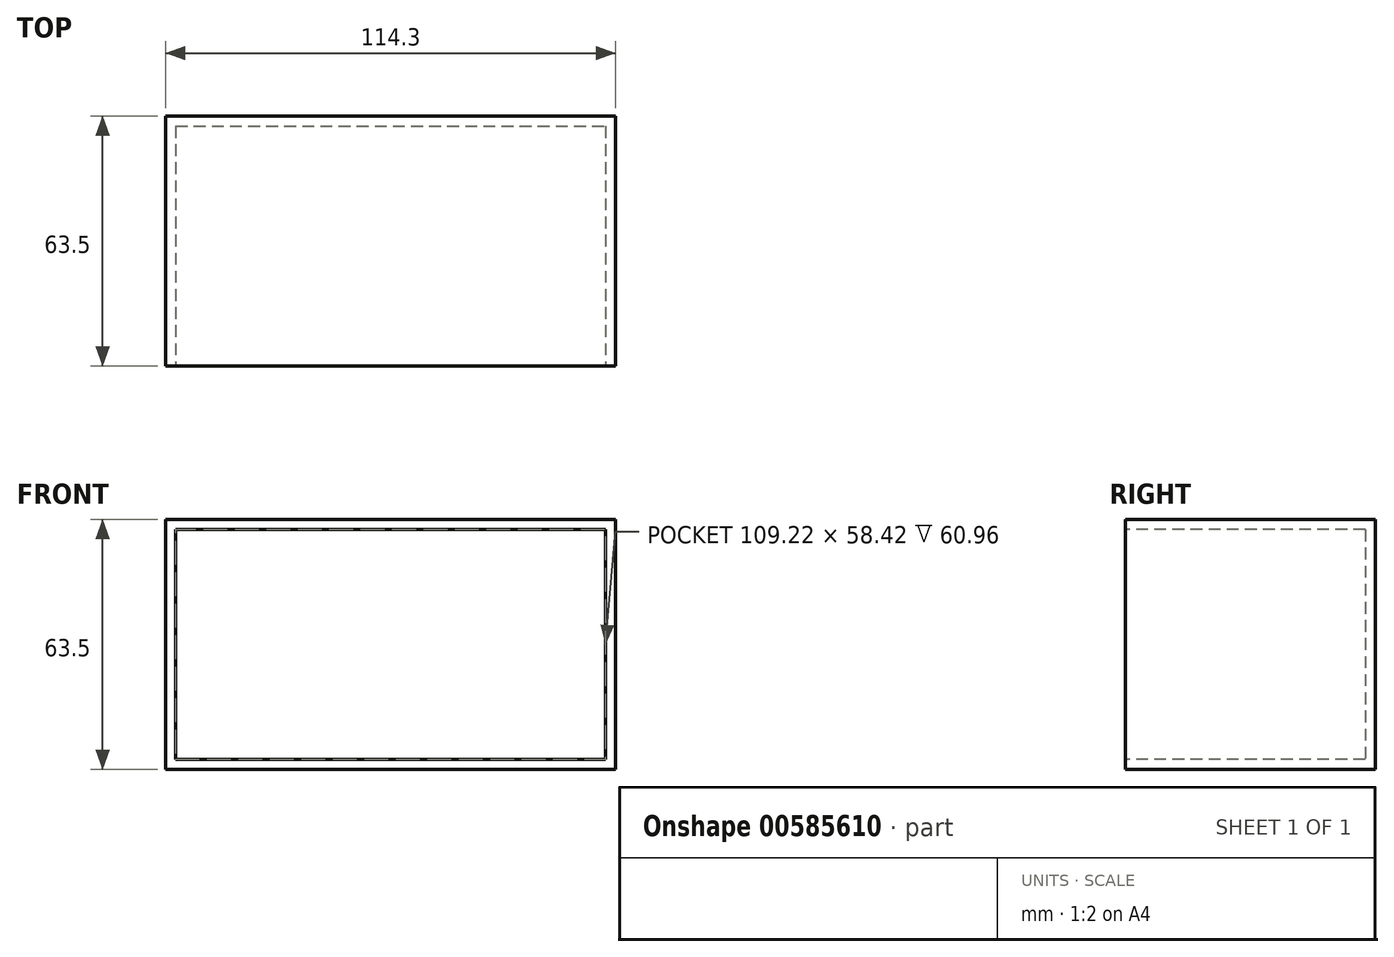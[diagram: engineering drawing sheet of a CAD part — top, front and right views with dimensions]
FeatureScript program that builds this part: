
annotation { "Feature Type Name" : "Feature", "Feature Type Description" : "" }
export const myFeature = defineFeature(function(context is Context, id is Id, definition is map)
    precondition{}
    {
        {
            var Q0;
            Q0=qCreatedBy(makeId("Top.planeOp"),FACE);
            var sketch = newSketch(context, id + "F0", { "sketchPlane" : qUnion([Q0])});
            skLineSegment(sketch, "E0.bottom", {"start": v(-57.15, 31.75) * mm, "end": v(57.15, 31.75) * mm});
            skLineSegment(sketch, "E0.top", {"start": v(-57.15, -31.75) * mm, "end": v(57.15, -31.75) * mm});
            skLineSegment(sketch, "E0.left", {"start": v(-57.15, 31.75) * mm, "end": v(-57.15, -31.75) * mm});
            skLineSegment(sketch, "E0.right", {"start": v(57.15, 31.75) * mm, "end": v(57.15, -31.75) * mm});
            skPoint(sketch, "E0.middle", {"position": v(0, 0) * mm});
            skSolve(sketch);
        }
        {
            var Q0;
            Q0=makeQuery(id+"F0.imprint","IMPRINT",FACE,{"disambiguationData":[TD([[makeQuery(id+"F0.imprint","IMPRINT",EDGE,{"derivedFrom":sQuery(id+"F0.wireOp",EDGE,"E0.bottom")}),-1.0]])]});
            extrude(context, id + "F1", {"entities" : qUnion([Q0]), "depth" : 63.5 * mm, "offsetDistance" : 25.4 * mm});
        }
        {
            var Q0;
            Q0=makeQuery(id+"F1.opExtrude","SWEPT_FACE",FACE,{"disambiguationData":[OSD([sQuery(id+"F0.wireOp",EDGE,"E0.top")])]});
            shell(context, id + "F2", {"entities" : qUnion([Q0]), "thickness" : 2.54 * mm});
        }
    });
